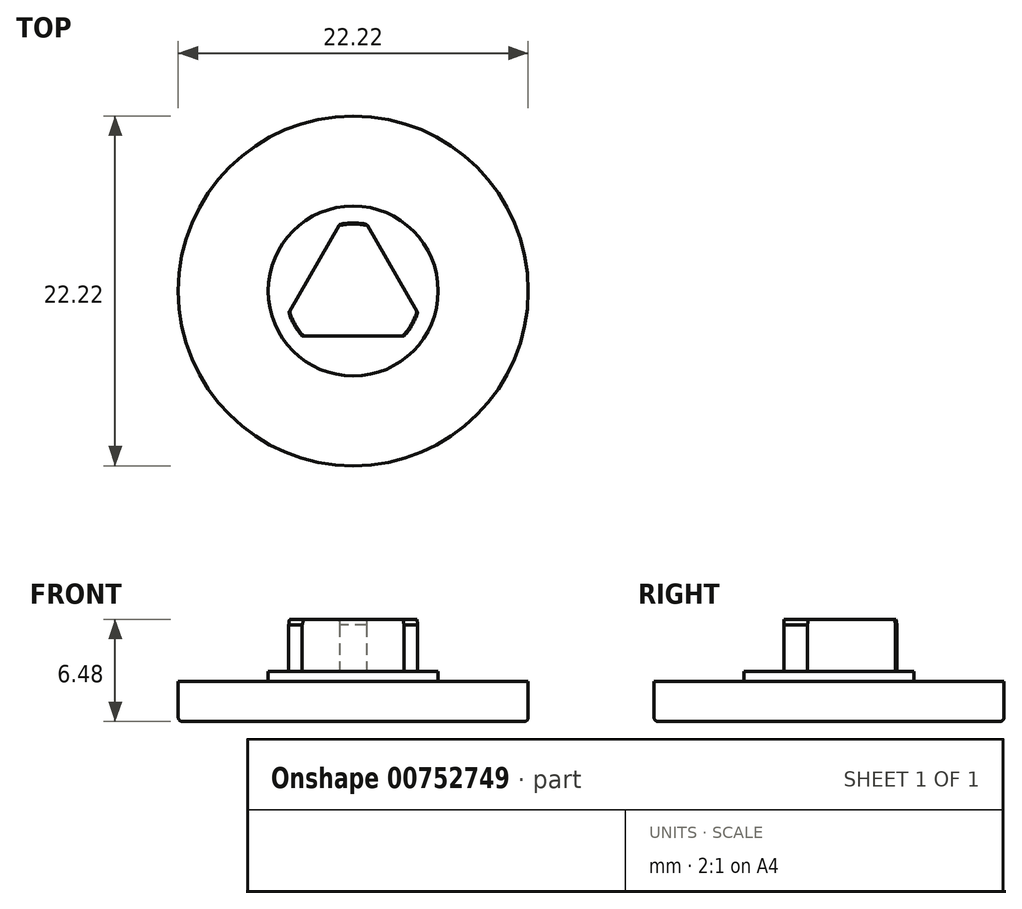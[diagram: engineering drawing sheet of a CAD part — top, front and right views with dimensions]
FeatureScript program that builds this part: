
annotation { "Feature Type Name" : "Feature", "Feature Type Description" : "" }
export const myFeature = defineFeature(function(context is Context, id is Id, definition is map)
    precondition{}
    {
        {
            var Q0;
            Q0=qCreatedBy(makeId("Top.planeOp"),FACE);
            var sketch = newSketch(context, id + "F0", { "sketchPlane" : qUnion([Q0])});
            skCircle(sketch, "E0", {"center": v(0, 0) * mm, "radius": 11.11 * mm});
            skSolve(sketch);
        }
        {
            var Q0;
            Q0 = qSketchRegion(id + "F0", true);
            extrude(context, id + "F1", {"entities" : qUnion([Q0]), "depth" : 2.54 * mm, "offsetDistance" : 25.4 * mm});
        }
        {
            var Q0;
            Q0=makeQuery(id+"F1.opExtrude","CAP_FACE",FACE,{"disambiguationData":[OSD([sQuery(id+"F0.wireOp",EDGE,"E0")])],"isStart":false});
            var sketch = newSketch(context, id + "F2", { "sketchPlane" : qUnion([Q0])});
            skCircle(sketch, "E1", {"center": v(0, 0) * mm, "radius": 5.4 * mm});
            skSolve(sketch);
        }
        {
            var Q0;
            Q0 = qSketchRegion(id + "F2", true);
            extrude(context, id + "F3", {"entities" : qUnion([Q0]), "operationType" : NewBodyOperationType.ADD, "depth" : 0.64 * mm, "offsetDistance" : 25.4 * mm});
        }
        {
            var Q0;
            Q0=makeQuery(id+"F3.opExtrude","CAP_FACE",FACE,{"disambiguationData":[OSD([sQuery(id+"F2.wireOp",EDGE,"E1")])],"isStart":false});
            var sketch = newSketch(context, id + "F4", { "sketchPlane" : qUnion([Q0])});
            skCircle(sketch, "E2.cCircle", {"center": v(0, 0) * mm, "radius": 2.86 * mm, "construction": true});
            skLineSegment(sketch, "E2.0", {"start": v(-4.1, -1.37) * mm, "end": v(-0.86, 4.23) * mm});
            skLineSegment(sketch, "E2.1", {"start": v(0.86, 4.23) * mm, "end": v(4.1, -1.37) * mm});
            skLineSegment(sketch, "E2.2", {"start": v(3.24, -2.86) * mm, "end": v(-3.24, -2.86) * mm});
            skPoint(sketch, "E2.0.midPoint", {"position": v(-2.47, 1.43) * mm});
            skCircle(sketch, "E3", {"center": v(0, 0) * mm, "radius": 5.72 * mm, "construction": true});
            skArc(sketch, "E4", {"start": v(-4.1, -1.37) * mm, "mid": v(-3.74, -2.16) * mm, "end": v(-3.24, -2.86) * mm});
            skPoint(sketch, "E5.orphan", {"position": v(-4.95, -2.86) * mm});
            skPoint(sketch, "E6.orphan", {"position": v(0, 5.72) * mm});
            skArc(sketch, "E7.trimOffspring", {"start": v(0.86, 4.23) * mm, "mid": v(0, 4.32) * mm, "end": v(-0.86, 4.23) * mm});
            skPoint(sketch, "E8.orphan", {"position": v(4.95, -2.86) * mm});
            skArc(sketch, "E9.trimOffspring", {"start": v(3.24, -2.86) * mm, "mid": v(3.74, -2.16) * mm, "end": v(4.1, -1.37) * mm});
            skSolve(sketch);
        }
        {
            var Q0;
            Q0 = qSketchRegion(id + "F4", true);
            extrude(context, id + "F5", {"entities" : qUnion([Q0]), "operationType" : NewBodyOperationType.ADD, "depth" : 3.3 * mm, "offsetDistance" : 25.4 * mm});
        }
        {
            var Q0;
            Q0=makeQuery(id+"F5.opExtrude","CAP_EDGE",EDGE,{"disambiguationData":[OSD([sQuery(id+"F4.wireOp",EDGE,"E9.trimOffspring")])],"isStart":false});
            var Q1;
            Q1=makeQuery(id+"F5.opExtrude","CAP_EDGE",EDGE,{"disambiguationData":[OSD([sQuery(id+"F4.wireOp",EDGE,"E4")])],"isStart":false});
            var Q2;
            Q2=makeQuery(id+"F5.opExtrude","CAP_EDGE",EDGE,{"disambiguationData":[OSD([sQuery(id+"F4.wireOp",EDGE,"E7.trimOffspring")])],"isStart":false});
            chamfer(context, id + "F6", {"entities" : qUnion([Q0, Q1, Q2]), "chamferType" : ChamferType.OFFSET_ANGLE, "width" : 0.06 * mm, "oppositeDirection" : false, "angle" : 80 * degree, "tangentPropagation" : true});
        }
        {
            var Q0;
            Q0=makeQuery(id+"F1.opExtrude","CAP_EDGE",EDGE,{"disambiguationData":[OSD([sQuery(id+"F0.wireOp",EDGE,"E0")])],"isStart":true});
            fillet(context, id + "F7", {"entities" : qUnion([Q0]), "radius" : 0.25 * mm, "tangentPropagation" : true, "allowEdgeOverflow" : false});
        }
    });
